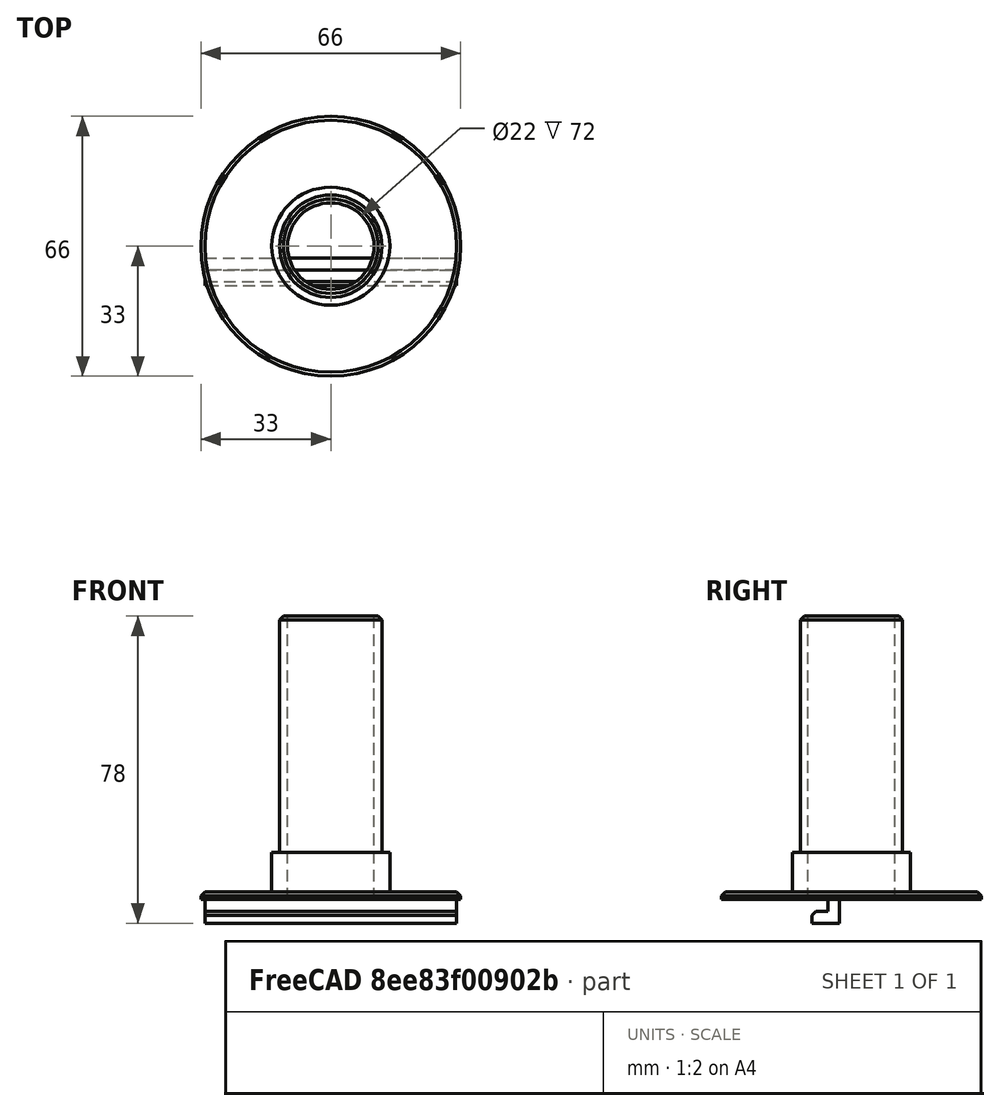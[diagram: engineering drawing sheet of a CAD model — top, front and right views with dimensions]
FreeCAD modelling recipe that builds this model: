
FCSTD DOCUMENT  (FreeCAD 0.16R6662 (Git))
Label: filamenthalter_base
License: CreativeCommons Attribution-ShareAlike
LicenseURL: http://creativecommons.org/licenses/by-sa/4.0/
objects: Part::Cylinder×4, Part::MultiFuse×4, Part::Chamfer×3, Part::Box×2, Part::Cut×1
note: 14 computed .brp shape members not serialized (recipe doc carries the construction recipe); baked Part::Feature solids carry a one-line shape summary decoded from their .brp

FEATURE [Part::Cylinder] Cylinder
  Angle = 360
  Height = 2
  Radius = 33
FEATURE [Part::Cylinder] Cylinder001
  Angle = 360
  Height = 11
  Placement = pos=(0,0,1) rot=(0,0,1;0rad)
  Radius = 15
FEATURE [Part::Cylinder] Cylinder002
  Angle = 360
  Height = 67
  Placement = pos=(0,0,10) rot=(0,0,1;0rad)
  Radius = 13
FEATURE [Part::Cylinder] Cylinder003
  Angle = 360
  Height = 80
  Placement = pos=(0,0,-1) rot=(0,0,1;0rad)
  Radius = 11
FEATURE [Part::Box] Box  label="Cube"
  Height = 7
  Length = 64
  Placement = pos=(-32,0,-6) rot=(0,0,1;0rad)
  Width = 3
FEATURE [Part::Box] Box001  label="Cube001"
  Height = 3
  Length = 64
  Placement = pos=(-32,-4,-6) rot=(0,0,1;0rad)
  Width = 6
FEATURE [Part::Chamfer] Chamfer
  Base = -> Box001
  Edges = 1 edges r=1: [Edge10]
FEATURE [Part::Chamfer] Chamfer001
  Base = -> Cylinder002
  Edges = 1 edges r=1: [Edge1]
  Placement = pos=(0,0,-5) rot=(0,0,1;0rad)
FEATURE [Part::MultiFuse] Fusion
  Shapes = -> [Cylinder,Cylinder001]
FEATURE [Part::MultiFuse] Fusion001
  Shapes = -> [Fusion,Chamfer001]
FEATURE [Part::Cut] Cut
  Base = -> Fusion001
  Tool = -> Cylinder003
FEATURE [Part::MultiFuse] Fusion002
  Placement = pos=(0,-6,0) rot=(0,0,1;0rad)
  Shapes = -> [Chamfer,Box]
FEATURE [Part::Chamfer] Chamfer002
  Base = -> Cut
  Edges = 1 edges r=1: [Edge1]
FEATURE [Part::MultiFuse] Fusion003
  Shapes = -> [Fusion002,Chamfer002]
